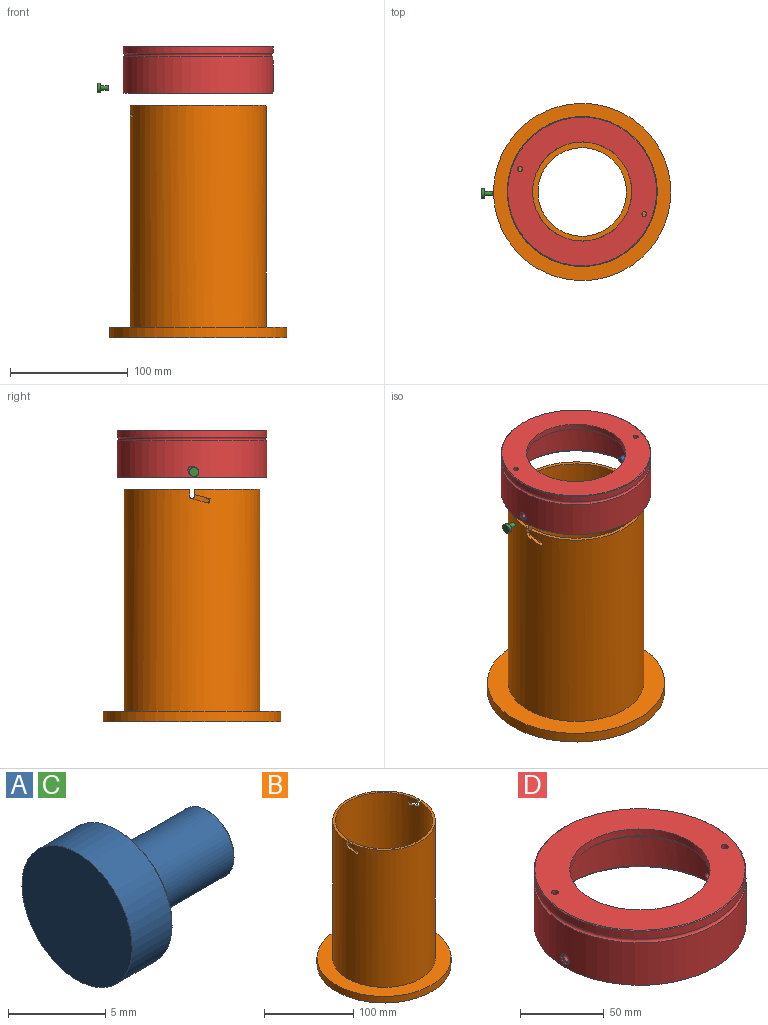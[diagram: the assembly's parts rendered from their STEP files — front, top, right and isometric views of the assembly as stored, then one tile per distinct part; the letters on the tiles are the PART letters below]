
ASSEMBLY  parts=4 mates=3
PART A: 7 faces, bbox 9.5x8x8 mm
  f0: cylinder r=2mm len=6.4mm, axis (-1,0,0), area 80.4mm2, adj f1,f6
  f1: plane 7.8x7.8mm, normal (1,0,0), area 35.2mm2, adj f0,f5
  f2: cylinder r=4mm len=8mm, axis (-1,0,0), area 72.9mm2, adj f3,f5
  f3: plane 8x8mm, normal (-1,0,0), area 50.3mm2, adj f2
  f4: plane 3.8x3.8mm, normal (1,0,0), area 11.3mm2, adj f6
  f5: cone r=4mm half-angle=45deg, axis (-1,0,0), area 3.5mm2, adj f1,f2
  f6: cone r=2mm half-angle=45deg, axis (-1,0,0), area 1.7mm2, adj f0,f4
PART B: 25 faces, bbox 150.2x150.2x197 mm
  f0: cylinder r=54.5mm len=188mm, axis (0,0,1), area 64210.4mm2, adj f1,f4,f5,f9,f10,f11,f12,f13
  f1: plane 114.84x54.5mm, normal (0,0,1), area 509.8mm2, adj f0,f2,f21,f23
  f2: cylinder r=57.5mm len=188mm, axis (0,0,1), area 67748.1mm2, adj f1,f5,f6,f9,f10,f11,f12,f13
  f3: cylinder r=37.5mm len=75mm, axis (0,0,1), area 2120.6mm2, adj f4,f8
  f4: plane 109x109mm, normal (0,0,1), area 4913.5mm2, adj f0,f3
  f5: plane 114.84x54.5mm, normal (0,0,1), area 509.8mm2, adj f0,f2,f22,f24
  f6: plane 150.2x150.2mm, normal (0,0,1), area 7331.7mm2, adj f2,f7
  f7: cylinder r=75.1mm len=150.2mm, axis (0,0,1), area 4246.8mm2, adj f6,f8
  f8: plane 150.2x150.2mm, normal (0,0,-1), area 13300.7mm2, adj f3,f7
  f9: plane 5x3mm, normal (0,-1,0), area 15mm2, adj f0,f2,f10,f22
  f10: cylinder r=2mm len=3.04mm, axis (1,0,0), area 8.5mm2, adj f0,f2,f9,f18
  f11: plane 3.47x3mm, normal (0,1,0), area 10.4mm2, adj f0,f2,f19,f21
  f12: plane 5x3mm, normal (0,1,0), area 15mm2, adj f0,f2,f13,f23
  f13: cylinder r=2mm len=3.04mm, axis (1,0,0), area 8.5mm2, adj f0,f2,f12,f15
  f14: plane 3.47x3mm, normal (0,-1,0), area 10.4mm2, adj f0,f2,f17,f24
  f15: bspline ~14.7x4.73mm, area 45mm2, adj f0,f2,f13,f16
  f16: plane 3.88x3.17mm, normal (0.25,-0.93,0.26), area 12mm2, adj f0,f2,f15,f17
  f17: bspline ~13.46x4.96mm, area 40.9mm2, adj f0,f2,f14,f16
  f18: bspline ~14.73x4.73mm, area 45mm2, adj f0,f2,f10,f20
  f19: bspline ~21.97x7.3mm, area 40.9mm2, adj f0,f2,f11,f20
  f20: plane 3.88x3.17mm, normal (-0.25,0.93,0.25), area 12mm2, adj f0,f2,f18,f19
  f21: plane 3.05x1mm, normal (0,0.71,0.71), area 4.2mm2, adj f0,f1,f2,f11
  f22: plane 3.05x1mm, normal (0,-0.71,0.71), area 4.2mm2, adj f0,f2,f5,f9
  f23: plane 3.05x1mm, normal (0,0.71,0.71), area 4.2mm2, adj f0,f1,f2,f12
  f24: plane 3.05x1mm, normal (0,-0.71,0.71), area 4.2mm2, adj f0,f2,f5,f14
PART C: same geometry as A
PART D: 25 faces, bbox 139.8x139.8x40 mm
  f0: cylinder r=57.6mm len=115.2mm, axis (0,0,-1), area 8660.7mm2, adj f1,f4,f7,f13,f18,f21,f23
  f1: plane 111.24x76mm, normal (0,0,-1), area 534.2mm2, adj f0,f2,f22,f24
  f2: cone r=52.5mm half-angle=45deg, axis (0,0,-1), area 948.1mm2, adj f1,f7,f8,f22,f24
  f3: cylinder r=63.5mm len=127mm, axis (0,0,-1), area 12291.4mm2, adj f5,f6,f14,f16
  f4: cylinder r=2mm len=5mm, axis (-1,0,0), area 62.8mm2, adj f0,f15
  f5: torus R=63.5mm, axis (0,0,-1), area 1851.9mm2, adj f3,f12
  f6: plane 127x127mm, normal (0,0,-1), area 1508.2mm2, adj f3,f18
  f7: plane 111.24x76mm, normal (0,0,-1), area 534.2mm2, adj f0,f2,f22,f24
  f8: cylinder r=52.5mm len=105mm, axis (0,0,-1), area 1979.2mm2, adj f2,f9
  f9: plane 105x105mm, normal (0,0,-1), area 2850.2mm2, adj f8,f19
  f10: cylinder r=42mm len=84mm, axis (0,0,-1), area 1319.5mm2, adj f11,f19
  f11: plane 126x126mm, normal (0,0,1), area 6899.5mm2, adj f10,f20,f22,f24
  f12: cylinder r=63.5mm len=127mm, axis (0,0,-1), area 2194.4mm2, adj f5,f20
  f13: cylinder r=2mm len=5mm, axis (-1,0,0), area 62.8mm2, adj f0,f17
  f14: cylinder r=3.5mm len=7mm, axis (-1,0,0), area 19.8mm2, adj f3,f15
  f15: plane 7x7mm, normal (1,0,0), area 25.9mm2, adj f4,f14
  f16: cylinder r=3.5mm len=7mm, axis (1,0,0), area 19.8mm2, adj f3,f17
  f17: plane 7x7mm, normal (-1,0,0), area 25.9mm2, adj f13,f16
  f18: cone r=57.6mm half-angle=45deg, axis (0,0,-1), area 1041.4mm2, adj f0,f6
  f19: cone r=42mm half-angle=45deg, axis (0,0,-1), area 377.6mm2, adj f9,f10
  f20: cone r=63.5mm half-angle=45deg, axis (0,0,-1), area 281mm2, adj f11,f12
  f21: cone r=0mm half-angle=59deg, axis (0,0,1), area 1.1mm2, adj f0,f22
  f22: cylinder r=2.1mm len=14mm, axis (0,0,1), area 183.5mm2, adj f1,f2,f7,f11,f21
  f23: cone r=0mm half-angle=59deg, axis (0,0,1), area 0mm2, adj f0,f24
  f24: cylinder r=2.1mm len=14mm, axis (0,0,1), area 184mm2, adj f1,f2,f7,f11,f23
PLACE A rot(axis=(0,0,1),180deg) t=(51.69,-42.51,16.3)mm
PLACE B t=(-7.91,-42.51,-196.7)mm
PLACE C t=(-90.51,-44.23,14.95)mm
PLACE D t=(-7.91,-42.51,10.3)mm
MATE planar D.f0 <-> B.f0  axis (0,0,1) through (-7.91,-42.51,50.3)mm
MATE planar C.f0 <-> D.f4  axis (1,0,0) through (-90.51,-44.23,14.95)mm
MATE planar A.f0 <-> D.f4  axis (1,0,0) through (54.69,-42.51,16.3)mm
